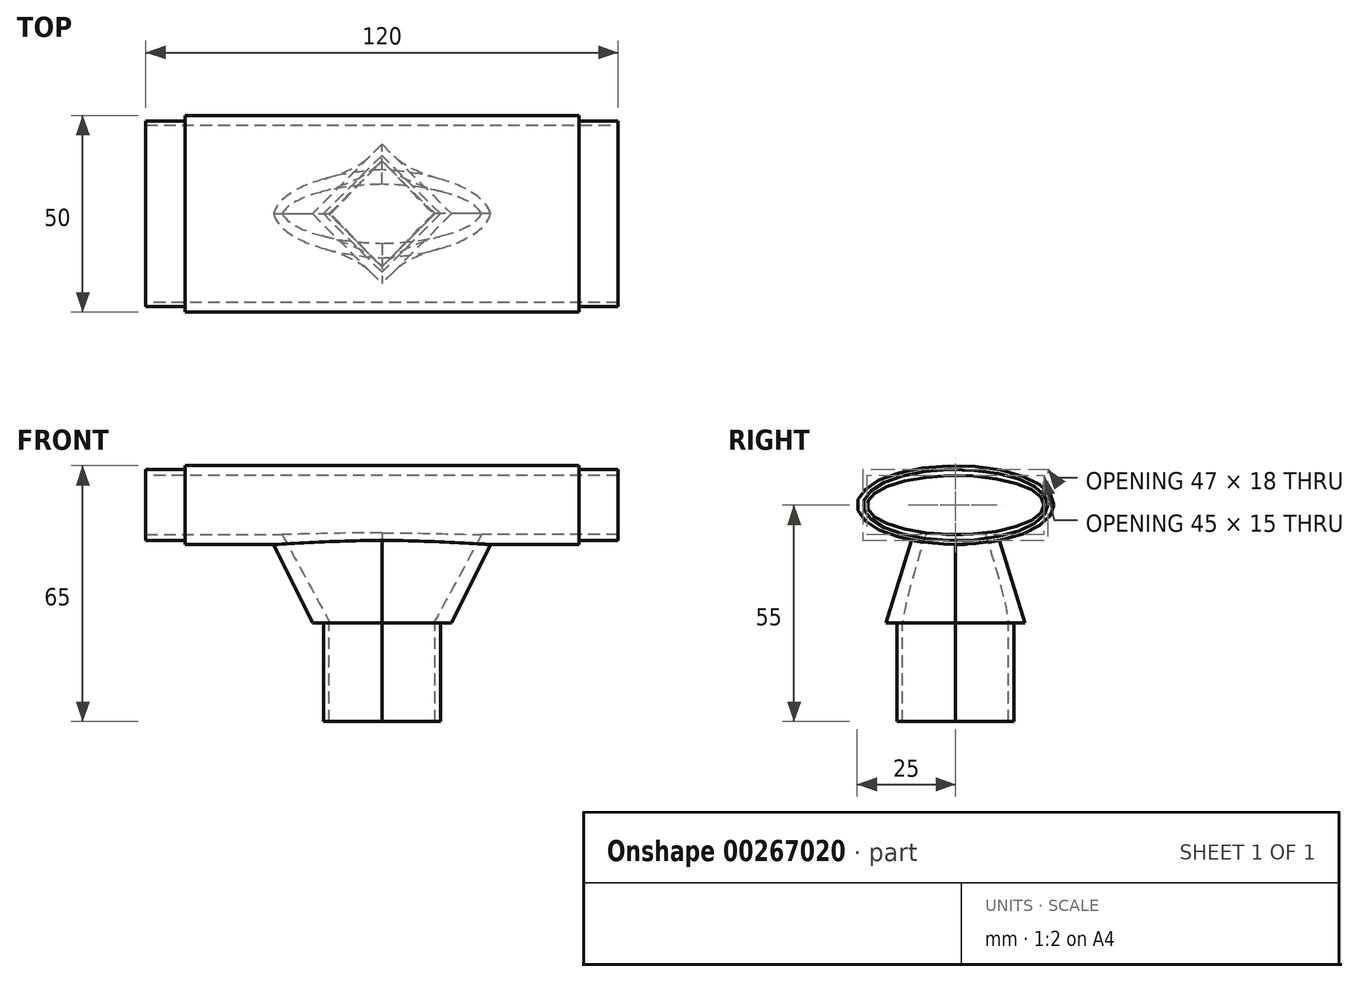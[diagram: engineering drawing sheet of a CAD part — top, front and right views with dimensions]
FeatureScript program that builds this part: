
annotation { "Feature Type Name" : "Feature", "Feature Type Description" : "" }
export const myFeature = defineFeature(function(context is Context, id is Id, definition is map)
    precondition{}
    {
        {
            var Q0;
            Q0=qCreatedBy(makeId("Top.planeOp"),FACE);
            var sketch = newSketch(context, id + "F0", { "sketchPlane" : qUnion([Q0])});
            skLineSegment(sketch, "E0.bottom", {"start": v(0, 17.68) * mm, "end": v(17.68, 0) * mm});
            skLineSegment(sketch, "E0.top", {"start": v(-17.68, 0) * mm, "end": v(0, -17.68) * mm});
            skLineSegment(sketch, "E0.left", {"start": v(0, 17.68) * mm, "end": v(-17.68, 0) * mm});
            skLineSegment(sketch, "E0.right", {"start": v(17.68, 0) * mm, "end": v(0, -17.68) * mm});
            skPoint(sketch, "E0.middle", {"position": v(0, 0) * mm});
            skSolve(sketch);
        }
        {
            var Q0;
            Q0=qCreatedBy(makeId("Top.planeOp"),FACE);
            cPlane(context, id + "F1", {"entities" : qUnion([Q0]), "cplaneType" : CPlaneType.OFFSET, "offset" : 25 * mm, "width" : 150 * mm, "height" : 150 * mm});
        }
        {
            var Q0;
            Q0=qCreatedBy(id+"F1.planeOp",FACE);
            var sketch = newSketch(context, id + "F2", { "sketchPlane" : qUnion([Q0])});
            skEllipse(sketch, "E1", {"center": v(0, 0) * mm, "majorRadius": 30 * mm, "minorRadius": 10 * mm, "majorAxis": v(1, 0)});
            skLineSegment(sketch, "E2.bottom", {"start": v(10, -10) * mm, "end": v(-10, -10) * mm, "construction": true});
            skLineSegment(sketch, "E2.top", {"start": v(10, 10) * mm, "end": v(-10, 10) * mm, "construction": true});
            skLineSegment(sketch, "E2.left", {"start": v(10, -10) * mm, "end": v(10, 10) * mm, "construction": true});
            skLineSegment(sketch, "E2.right", {"start": v(-10, -10) * mm, "end": v(-10, 10) * mm, "construction": true});
            skSolve(sketch);
        }
        {
            var Q0;
            Q0=qCreatedBy(makeId("Right.planeOp"),FACE);
            cPlane(context, id + "F3", {"entities" : qUnion([Q0]), "cplaneType" : CPlaneType.OFFSET, "offset" : 50 * mm, "width" : 150 * mm, "height" : 150 * mm});
        }
        {
            var Q0;
            Q0=qCreatedBy(id+"F3.planeOp",FACE);
            var sketch = newSketch(context, id + "F4", { "sketchPlane" : qUnion([Q0])});
            skEllipse(sketch, "E3", {"center": v(0, 30) * mm, "majorRadius": 25 * mm, "minorRadius": 10 * mm, "majorAxis": v(1, 0)});
            skSolve(sketch);
        }
        {
            var Q0;
            Q0=makeQuery(id+"F2.imprint","IMPRINT",FACE,{"disambiguationData":[TD([[makeQuery(id+"F2.imprint","IMPRINT",EDGE,{"derivedFrom":sQuery(id+"F2.wireOp",EDGE,"E1")}),1.0]])]});
            var Q1;
            Q1=makeQuery(id+"F0.imprint","IMPRINT",FACE,{"disambiguationData":[TD([[makeQuery(id+"F0.imprint","IMPRINT",EDGE,{"derivedFrom":sQuery(id+"F0.wireOp",EDGE,"E0.bottom")}),-1.0]])]});
            loft(context, id + "F5", {"sheetProfilesArray" : [{ "sheetProfileEntities" : qUnion([Q0]) }, { "sheetProfileEntities" : qUnion([Q1]) }]});
        }
        {
            var Q0;
            Q0=makeQuery(id+"F4.imprint","IMPRINT",FACE,{"disambiguationData":[TD([[makeQuery(id+"F4.imprint","IMPRINT",EDGE,{"derivedFrom":sQuery(id+"F4.wireOp",EDGE,"E3")}),1.0]])]});
            extrude(context, id + "F6", {"entities" : qUnion([Q0]), "operationType" : NewBodyOperationType.ADD, "oppositeDirection" : true, "depth" : 100 * mm});
        }
        {
            var Q0;
            Q0=makeQuery(id+"F5.opLoft","CAP_FACE",FACE,{"disambiguationData":[OSD([makeQuery(id+"F0.imprint","IMPRINT",FACE,{"disambiguationData":[TD([[makeQuery(id+"F0.imprint","IMPRINT",EDGE,{"derivedFrom":sQuery(id+"F0.wireOp",EDGE,"E0.bottom")}),-1.0]])]})])],"isStart":true});
            shell(context, id + "F7", {"entities" : qUnion([Q0]), "thickness" : 3 * mm});
        }
        {
            var Q0;
            Q0=makeQuery(id+"F6.opExtrude","CAP_FACE",FACE,{"disambiguationData":[OSD([sQuery(id+"F4.wireOp",EDGE,"E3")])],"isStart":true});
            var sketch = newSketch(context, id + "F8", { "sketchPlane" : qUnion([Q0])});
            skEllipse(sketch, "E4", {"center": v(0, 30) * mm, "majorRadius": 22.5 * mm, "minorRadius": 7.5 * mm, "majorAxis": v(1, 0)});
            skSolve(sketch);
        }
        {
            var Q0;
            Q0 = qSketchRegion(id + "F8", true);
            extrude(context, id + "F9", {"entities" : qUnion([Q0]), "operationType" : NewBodyOperationType.REMOVE, "endBound" : BoundingType.THROUGH_ALL, "oppositeDirection" : true, "depth" : 25 * mm});
        }
        {
            var Q0;
            Q0=makeQuery(id+"F6.opExtrude","CAP_FACE",FACE,{"disambiguationData":[OSD([sQuery(id+"F4.wireOp",EDGE,"E3")])],"isStart":true});
            var sketch = newSketch(context, id + "F10", { "sketchPlane" : qUnion([Q0])});
            skEllipse(sketch, "E5", {"center": v(0, 30) * mm, "majorRadius": 23.5 * mm, "minorRadius": 9 * mm, "majorAxis": v(1, 0)});
            skSolve(sketch);
        }
        {
            var Q0;
            Q0=makeQuery(id+"F10.imprint","IMPRINT",FACE,{"disambiguationData":[TD([[makeQuery(id+"F10.imprint","IMPRINT",EDGE,{"derivedFrom":sQuery(id+"F10.wireOp",EDGE,"E5")}),1.0]])]});
            extrude(context, id + "F11", {"entities" : qUnion([Q0]), "operationType" : NewBodyOperationType.ADD, "depth" : 10 * mm});
        }
        {
            var Q0;
            Q0=makeQuery(id+"F6.opExtrude","CAP_FACE",FACE,{"disambiguationData":[OSD([sQuery(id+"F4.wireOp",EDGE,"E3")])],"isStart":false});
            var sketch = newSketch(context, id + "F12", { "sketchPlane" : qUnion([Q0])});
            skEllipse(sketch, "E6", {"center": v(0, 30) * mm, "majorRadius": 23.5 * mm, "minorRadius": 9 * mm, "majorAxis": v(1, 0)});
            skSolve(sketch);
        }
        {
            var Q0;
            Q0=makeQuery(id+"F12.imprint","IMPRINT",FACE,{"disambiguationData":[TD([[makeQuery(id+"F12.imprint","IMPRINT",EDGE,{"derivedFrom":sQuery(id+"F12.wireOp",EDGE,"E6")}),1.0]])]});
            extrude(context, id + "F13", {"entities" : qUnion([Q0]), "operationType" : NewBodyOperationType.ADD, "depth" : 10 * mm});
        }
        {
            var Q0;
            Q0=makeQuery(id+"F5.opLoft","CAP_FACE",FACE,{"disambiguationData":[OSD([makeQuery(id+"F0.imprint","IMPRINT",FACE,{"disambiguationData":[TD([[makeQuery(id+"F0.imprint","IMPRINT",EDGE,{"derivedFrom":sQuery(id+"F0.wireOp",EDGE,"E0.bottom")}),-1.0]])]})])],"isStart":true});
            var sketch = newSketch(context, id + "F14", { "sketchPlane" : qUnion([Q0])});
            skLineSegment(sketch, "E7.bottom", {"start": v(14.85, 0) * mm, "end": v(0, 14.85) * mm});
            skLineSegment(sketch, "E7.top", {"start": v(0, -14.85) * mm, "end": v(-14.85, 0) * mm});
            skLineSegment(sketch, "E7.left", {"start": v(14.85, 0) * mm, "end": v(0, -14.85) * mm});
            skLineSegment(sketch, "E7.right", {"start": v(0, 14.85) * mm, "end": v(-14.85, 0) * mm});
            skPoint(sketch, "E7.middle", {"position": v(0, 0) * mm});
            skLineSegment(sketch, "E8.bottom", {"start": v(0, 17.68) * mm, "end": v(17.68, 0) * mm});
            skLineSegment(sketch, "E8.top", {"start": v(-17.68, 0) * mm, "end": v(0, -17.68) * mm});
            skLineSegment(sketch, "E8.left", {"start": v(0, 17.68) * mm, "end": v(-17.68, 0) * mm});
            skLineSegment(sketch, "E8.right", {"start": v(17.68, 0) * mm, "end": v(0, -17.68) * mm});
            skLineSegment(sketch, "E9.bottom", {"start": v(0, 13.44) * mm, "end": v(13.44, 0) * mm});
            skLineSegment(sketch, "E9.top", {"start": v(-13.44, 0) * mm, "end": v(0, -13.44) * mm});
            skLineSegment(sketch, "E9.left", {"start": v(0, 13.44) * mm, "end": v(-13.44, 0) * mm});
            skLineSegment(sketch, "E9.right", {"start": v(13.44, 0) * mm, "end": v(0, -13.44) * mm});
            skSolve(sketch);
        }
        {
            var Q0;
            Q0=makeQuery(id+"F14.imprint","IMPRINT",FACE,{"disambiguationData":[TD([[makeQuery(id+"F14.imprint","IMPRINT",EDGE,{"derivedFrom":sQuery(id+"F14.wireOp",EDGE,"E7.bottom")}),1.0]])]});
            extrude(context, id + "F15", {"entities" : qUnion([Q0]), "operationType" : NewBodyOperationType.ADD, "depth" : 25 * mm});
        }
    });
